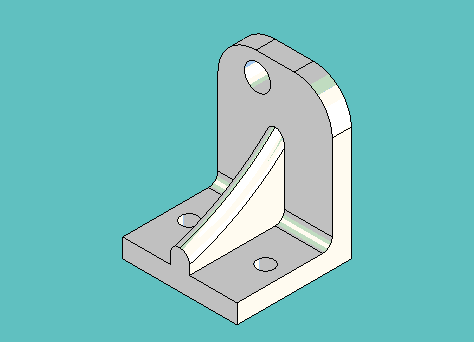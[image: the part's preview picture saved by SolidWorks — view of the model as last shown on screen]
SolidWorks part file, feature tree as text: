
SOLIDWORKS PART (.sldprt)
format: sldprt  version: not decoded by parser v0  size: 810,496 bytes
history: native  units: mm
features: sketch x4, extrude x4, boolean_combine x3, fillet x2, material x1, plane x1 (+11 scaffold rows collapsed)
feature tree (26):
  scaffold x11  (default folders/planes/origin — collapsed)
  material  "Material <not specified>"
  sketch  "Sketch1"  dims[D1=25.4mm D2=25.4mm D3=9.398mm D4=3.175mm D5=19.05mm D6=3.175mm D7=9.398mm D8=1.6002mm D9=19.05mm D10=1.6002mm]
  extrude  "Extrude1"  Depth=19.05mm
  sketch  "Sketch2"  dims[D1=4.3688mm D2=12.446mm D3=21.59mm]
  extrude  "Extrude2"  [1 undecoded]
  boolean_combine  "Combine1"
  plane  "Plane1"
  sketch  "Sketch3"  dims[D4=38.1mm D1=12.7mm D2=~0.79375mm D3=3.175mm]
  extrude  "Extrude3"  Depth=1.5875mm
  boolean_combine  "Combine2"
  sketch  "Sketch4"  dims[D1=~2.77622mm D2=11.1125mm D3=6.35mm]
  extrude  "Extrude4"  [1 undecoded]
  boolean_combine  "Combine3"
  fillet  "Fillet1"  Radius=1.5875mm
  fillet  "Fillet2"  Radius=6.35mm
decode coverage: 8 of 13 modeling features carry decoded parameters
note: ~ marks probable driven/reference dimensions
note: 2 parameter values undecoded
note: suppression state not decoded; provenance and decode notes live in map.json
